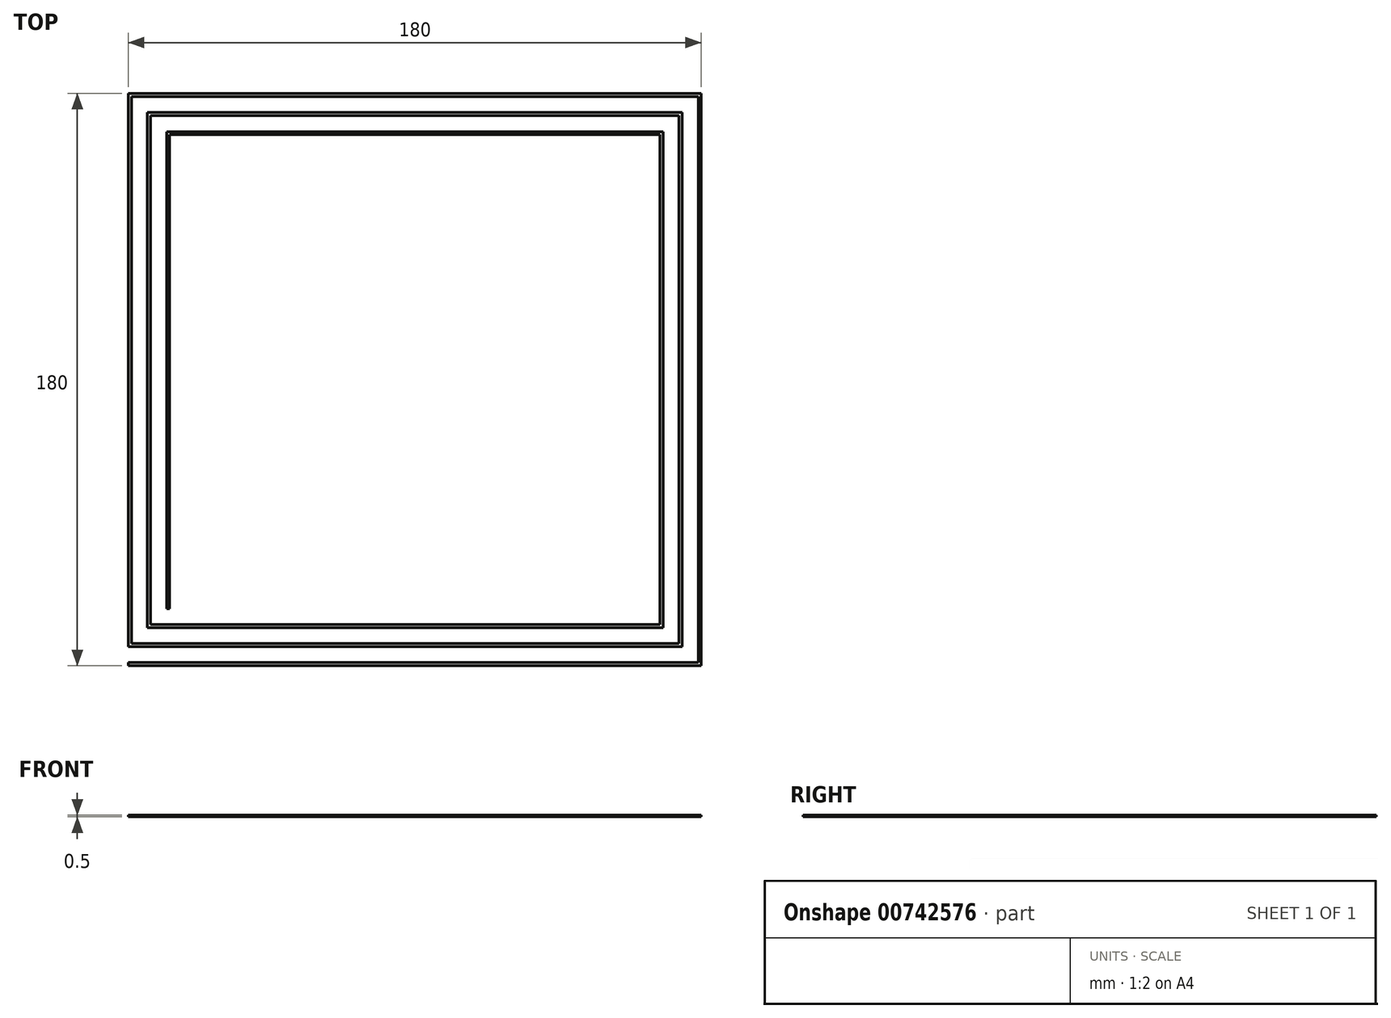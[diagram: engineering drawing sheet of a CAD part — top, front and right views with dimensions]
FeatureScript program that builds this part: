
annotation { "Feature Type Name" : "Feature", "Feature Type Description" : "" }
export const myFeature = defineFeature(function(context is Context, id is Id, definition is map)
    precondition{}
    {
        {
            var Q0;
            Q0=qCreatedBy(makeId("Top.planeOp"),FACE);
            var sketch = newSketch(context, id + "F0", { "sketchPlane" : qUnion([Q0])});
            skLineSegment(sketch, "E0.bottom", {"start": v(-90, 90) * mm, "end": v(90, 90) * mm, "construction": true});
            skLineSegment(sketch, "E0.top", {"start": v(-90, -90) * mm, "end": v(90, -90) * mm, "construction": true});
            skLineSegment(sketch, "E0.left", {"start": v(-90, 90) * mm, "end": v(-90, -90) * mm, "construction": true});
            skLineSegment(sketch, "E0.right", {"start": v(90, 90) * mm, "end": v(90, -90) * mm, "construction": true});
            skPoint(sketch, "E0.middle", {"position": v(0, 0) * mm});
            skLineSegment(sketch, "E1.bottom", {"start": v(-90, -90) * mm, "end": v(90, -90) * mm});
            skLineSegment(sketch, "E1.top", {"start": v(-90, -89) * mm, "end": v(89, -89) * mm});
            skLineSegment(sketch, "E1.left", {"start": v(-90, -90) * mm, "end": v(-90, -89) * mm});
            skLineSegment(sketch, "E1.right", {"start": v(90, -90) * mm, "end": v(90, -89) * mm});
            skLineSegment(sketch, "E2.bottom", {"start": v(90, -90) * mm, "end": v(89, -90) * mm});
            skLineSegment(sketch, "E2.top", {"start": v(90, 90) * mm, "end": v(89, 90) * mm});
            skLineSegment(sketch, "E2.left", {"start": v(90, -90) * mm, "end": v(90, 90) * mm});
            skLineSegment(sketch, "E2.right", {"start": v(89, -89) * mm, "end": v(89, 89) * mm});
            skLineSegment(sketch, "E3.bottom", {"start": v(90, 90) * mm, "end": v(-90, 90) * mm});
            skLineSegment(sketch, "E3.top", {"start": v(89, 89) * mm, "end": v(-89, 89) * mm});
            skLineSegment(sketch, "E3.left", {"start": v(90, 90) * mm, "end": v(90, 89) * mm});
            skLineSegment(sketch, "E3.right", {"start": v(-90, 90) * mm, "end": v(-90, 89) * mm});
            skLineSegment(sketch, "E4.bottom", {"start": v(-90, 90) * mm, "end": v(-89, 90) * mm});
            skLineSegment(sketch, "E4.top", {"start": v(-90, -84) * mm, "end": v(-89, -84) * mm});
            skLineSegment(sketch, "E4.left", {"start": v(-90, 90) * mm, "end": v(-90, -84) * mm});
            skLineSegment(sketch, "E4.right", {"start": v(-89, 89) * mm, "end": v(-89, -83) * mm});
            skLineSegment(sketch, "E5.bottom", {"start": v(-90, -84) * mm, "end": v(84, -84) * mm});
            skLineSegment(sketch, "E5.top", {"start": v(-89, -83) * mm, "end": v(83, -83) * mm});
            skLineSegment(sketch, "E5.left", {"start": v(-90, -84) * mm, "end": v(-90, -83) * mm});
            skLineSegment(sketch, "E5.right", {"start": v(84, -84) * mm, "end": v(84, -83) * mm});
            skLineSegment(sketch, "E6.bottom", {"start": v(84, -84) * mm, "end": v(83, -84) * mm});
            skLineSegment(sketch, "E6.top", {"start": v(84, 84) * mm, "end": v(83, 84) * mm});
            skLineSegment(sketch, "E6.left", {"start": v(84, -84) * mm, "end": v(84, 84) * mm});
            skLineSegment(sketch, "E6.right", {"start": v(83, -83) * mm, "end": v(83, 83) * mm});
            skLineSegment(sketch, "E7.bottom", {"start": v(84, 84) * mm, "end": v(-84, 84) * mm});
            skLineSegment(sketch, "E7.top", {"start": v(83, 83) * mm, "end": v(-83, 83) * mm});
            skLineSegment(sketch, "E7.left", {"start": v(84, 84) * mm, "end": v(84, 83) * mm});
            skLineSegment(sketch, "E7.right", {"start": v(-84, 84) * mm, "end": v(-84, 83) * mm});
            skLineSegment(sketch, "E8.bottom", {"start": v(-84, 84) * mm, "end": v(-83, 84) * mm});
            skLineSegment(sketch, "E8.top", {"start": v(-84, -78) * mm, "end": v(-83, -78) * mm});
            skLineSegment(sketch, "E8.left", {"start": v(-84, 84) * mm, "end": v(-84, -78) * mm});
            skLineSegment(sketch, "E8.right", {"start": v(-83, 83) * mm, "end": v(-83, -77) * mm});
            skLineSegment(sketch, "E9.bottom", {"start": v(-84, -78) * mm, "end": v(78, -78) * mm});
            skLineSegment(sketch, "E9.top", {"start": v(-83, -77) * mm, "end": v(77, -77) * mm});
            skLineSegment(sketch, "E9.left", {"start": v(-84, -78) * mm, "end": v(-84, -77) * mm});
            skLineSegment(sketch, "E9.right", {"start": v(78, -78) * mm, "end": v(78, -77) * mm});
            skLineSegment(sketch, "E10.bottom", {"start": v(78, -78) * mm, "end": v(77, -78) * mm});
            skLineSegment(sketch, "E10.top", {"start": v(78, 78) * mm, "end": v(77, 78) * mm});
            skLineSegment(sketch, "E10.left", {"start": v(78, -78) * mm, "end": v(78, 78) * mm});
            skLineSegment(sketch, "E10.right", {"start": v(77, -77) * mm, "end": v(77, 77) * mm});
            skLineSegment(sketch, "E11.bottom", {"start": v(78, 78) * mm, "end": v(-78, 78) * mm});
            skLineSegment(sketch, "E11.top", {"start": v(77, 77) * mm, "end": v(-77, 77) * mm});
            skLineSegment(sketch, "E11.left", {"start": v(78, 78) * mm, "end": v(78, 77) * mm});
            skLineSegment(sketch, "E11.right", {"start": v(-78, 78) * mm, "end": v(-78, 77) * mm});
            skLineSegment(sketch, "E12.bottom", {"start": v(-78, 78) * mm, "end": v(-77, 78) * mm});
            skLineSegment(sketch, "E12.top", {"start": v(-78, -72) * mm, "end": v(-77, -72) * mm});
            skLineSegment(sketch, "E12.left", {"start": v(-78, 78) * mm, "end": v(-78, -72) * mm});
            skLineSegment(sketch, "E12.right", {"start": v(-77, 77) * mm, "end": v(-77, -72) * mm});
            skSolve(sketch);
        }
        {
            var Q0;
            Q0 = qSketchRegion(id + "F0", true);
            extrude(context, id + "F1", {"entities" : qUnion([Q0]), "depth" : 0.5 * mm, "offsetDistance" : 25 * mm});
        }
    });
